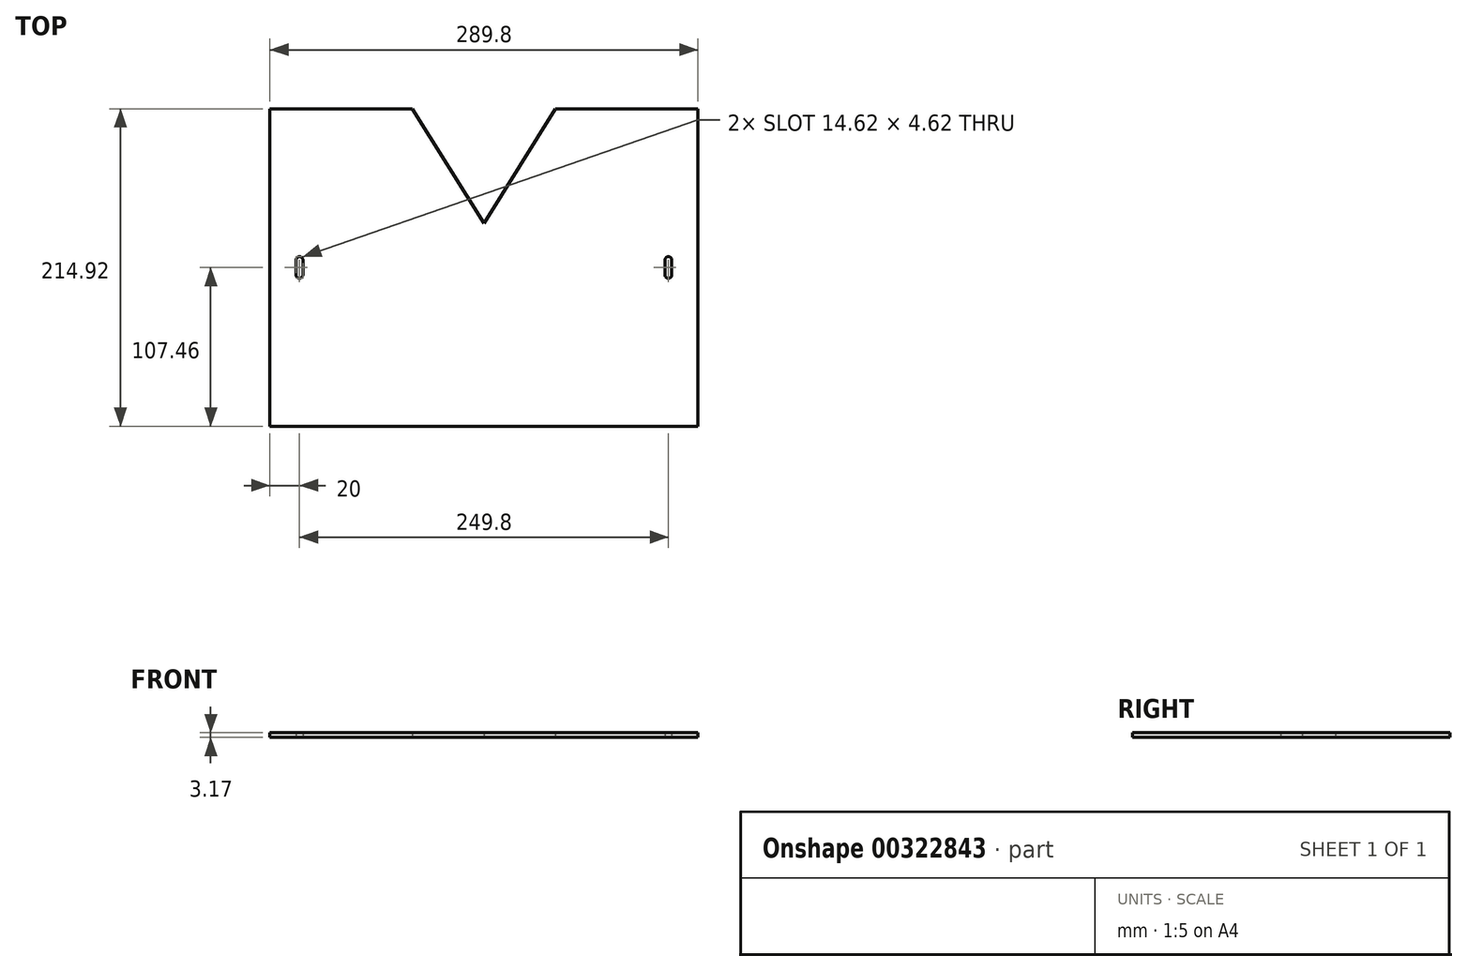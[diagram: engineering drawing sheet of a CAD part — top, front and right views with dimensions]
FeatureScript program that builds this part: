
annotation { "Feature Type Name" : "Feature", "Feature Type Description" : "" }
export const myFeature = defineFeature(function(context is Context, id is Id, definition is map)
    precondition{}
    {
        {
            var Q0;
            Q0=qCreatedBy(makeId("Top.planeOp"),FACE);
            var sketch = newSketch(context, id + "F0", { "sketchPlane" : qUnion([Q0])});
            skLineSegment(sketch, "E0.bottom", {"start": v(144.9, -107.46) * mm, "end": v(-144.9, -107.46) * mm});
            skLineSegment(sketch, "E0.top", {"start": v(144.9, 107.46) * mm, "end": v(-144.9, 107.46) * mm});
            skLineSegment(sketch, "E0.left", {"start": v(144.9, -107.46) * mm, "end": v(144.9, 107.46) * mm});
            skLineSegment(sketch, "E0.right", {"start": v(-144.9, -107.46) * mm, "end": v(-144.9, 107.46) * mm});
            skPoint(sketch, "E0.middle", {"position": v(0, 0) * mm});
            skLineSegment(sketch, "E1", {"start": v(-144.9, 0) * mm, "end": v(-124.9, 0) * mm});
            skPoint(sketch, "E1.endSnap0", {"position": v(-144.9, 0) * mm});
            skLineSegment(sketch, "E2", {"start": v(-124.9, 0) * mm, "end": v(-144.9, 0) * mm});
            skPoint(sketch, "E3.endSnap0", {"position": v(144.9, 0) * mm});
            skLineSegment(sketch, "E4.bottom", {"start": v(-122.59, -5) * mm, "end": v(-127.21, -5) * mm});
            skLineSegment(sketch, "E4.top", {"start": v(-122.59, 5) * mm, "end": v(-127.21, 5) * mm});
            skLineSegment(sketch, "E4.left", {"start": v(-122.59, -5) * mm, "end": v(-122.59, 5) * mm});
            skLineSegment(sketch, "E4.right", {"start": v(-127.21, -5) * mm, "end": v(-127.21, 5) * mm});
            skPoint(sketch, "E4.middle", {"position": v(-124.9, 0) * mm});
            skCircle(sketch, "E5", {"center": v(-124.9, -5) * mm, "radius": 2.31 * mm});
            skCircle(sketch, "E6", {"center": v(-124.9, 5) * mm, "radius": 2.31 * mm});
            skLineSegment(sketch, "E7", {"start": v(0, 0) * mm, "end": v(0, 22.19) * mm});
            skCircle(sketch, "E8.MirrorC", {"center": v(124.9, 5) * mm, "radius": 2.31 * mm});
            skCircle(sketch, "E9.MirrorC", {"center": v(124.9, -5) * mm, "radius": 2.31 * mm});
            skLineSegment(sketch, "E10.MirrorCS", {"start": v(122.59, -5) * mm, "end": v(122.59, 5) * mm});
            skLineSegment(sketch, "E11.MirrorCS", {"start": v(127.21, -5) * mm, "end": v(127.21, 5) * mm});
            skPoint(sketch, "E3.end.orphan", {"position": v(124.9, 0) * mm});
            skLineSegment(sketch, "E12", {"start": v(0, 0) * mm, "end": v(0, 30) * mm});
            skPoint(sketch, "E12.endSnap0", {"position": v(0, 107.46) * mm});
            skLineSegment(sketch, "E13", {"start": v(0, 30) * mm, "end": v(48.42, 107.46) * mm});
            skLineSegment(sketch, "E14.MirrorCS", {"start": v(0, 30) * mm, "end": v(-48.42, 107.46) * mm});
            skSolve(sketch);
        }
        {
            var Q0;
            {var subQ12=sQuery(id+"F0.wireOp",EDGE,"E0.bottom");Q0=makeQuery(id+"F0.imprint","IMPRINT",FACE,{"disambiguationData":[TD([[makeQuery(id+"F0.imprint","IMPRINT",EDGE,{"derivedFrom":subQ12}),-1.0]])]});}
            extrude(context, id + "F1", {"entities" : qUnion([Q0]), "depth" : 3.17 * mm});
        }
    });
